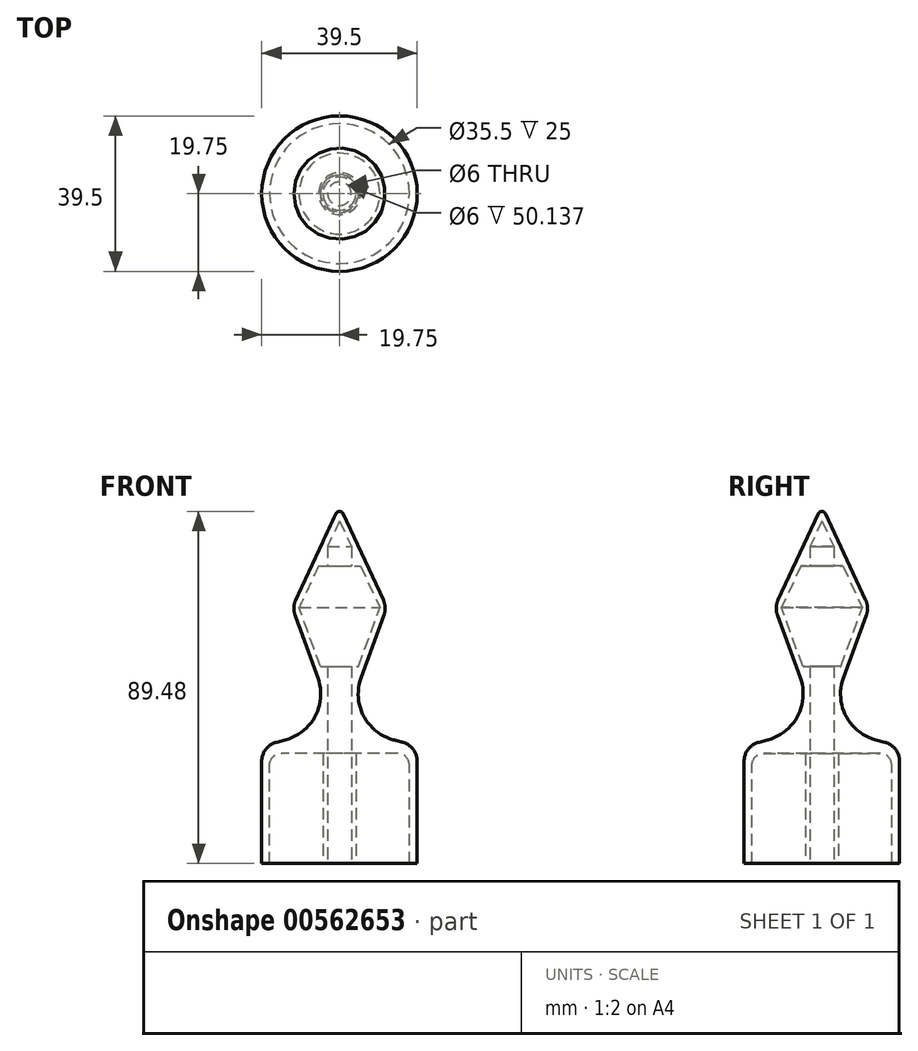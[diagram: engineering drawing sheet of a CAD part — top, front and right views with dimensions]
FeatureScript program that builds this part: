
annotation { "Feature Type Name" : "Feature", "Feature Type Description" : "" }
export const myFeature = defineFeature(function(context is Context, id is Id, definition is map)
    precondition{}
    {
        {
            var Q0;
            Q0=qCreatedBy(makeId("Front.planeOp"),FACE);
            var sketch = newSketch(context, id + "F0", { "sketchPlane" : qUnion([Q0])});
            skLineSegment(sketch, "E0.top", {"start": v(17.75, -35.14) * mm, "end": v(19.75, -35.14) * mm});
            skLineSegment(sketch, "E0.left", {"start": v(0, 0) * mm, "end": v(0, -7.14) * mm});
            skLineSegment(sketch, "E0.right", {"start": v(19.75, -5.3) * mm, "end": v(19.75, -35.14) * mm});
            skLineSegment(sketch, "E1", {"start": v(0, 0) * mm, "end": v(19.75, -5.3) * mm});
            skLineSegment(sketch, "E2.top", {"start": v(0, -7.14) * mm, "end": v(17.75, -7.14) * mm});
            skLineSegment(sketch, "E2.right", {"start": v(17.75, -35.14) * mm, "end": v(17.75, -7.14) * mm});
            skSolve(sketch);
        }
        {
            var Q0;
            Q0=qCreatedBy(makeId("Front.planeOp"),FACE);
            var sketch = newSketch(context, id + "F1", { "sketchPlane" : qUnion([Q0])});
            skLineSegment(sketch, "E3", {"start": v(0, 237.23) * mm, "end": v(0, -268.52) * mm});
            skSolve(sketch);
        }
        {
            var Q0;
            Q0 = qSketchRegion(id + "F0", true);
            var Q1;
            Q1=sQuery(id+"F1.wireOp",EDGE,"E3");
            revolve(context, id + "F2", {"surfaceOperationType" : NewSurfaceOperationType.NEW, "entities" : qUnion([Q0]), "axis" : qUnion([Q1]), "revolveType" : RevolveType.FULL});
        }
        {
            var Q0;
            Q0=qCreatedBy(makeId("Front.planeOp"),FACE);
            var sketch = newSketch(context, id + "F3", { "sketchPlane" : qUnion([Q0])});
            skLineSegment(sketch, "E4", {"start": v(0, -3) * mm, "end": v(0, 54.34) * mm});
            skLineSegment(sketch, "E5", {"start": v(0.9, 53.76) * mm, "end": v(12, 29.97) * mm});
            skLineSegment(sketch, "E6", {"start": v(12, 29.97) * mm, "end": v(0, -3) * mm});
            skArc(sketch, "E7", {"start": v(0.9, 53.76) * mm, "mid": v(0.54, 54.18) * mm, "end": v(0, 54.34) * mm});
            skSolve(sketch);
        }
        {
            var Q0;
            Q0 = qSketchRegion(id + "F3", true);
            var Q1;
            Q1=sQuery(id+"F3.wireOp",EDGE,"E4");
            revolve(context, id + "F4", {"operationType" : NewBodyOperationType.ADD, "surfaceOperationType" : NewSurfaceOperationType.NEW, "entities" : qUnion([Q0]), "axis" : qUnion([Q1]), "revolveType" : RevolveType.FULL});
        }
        {
            var Q0;
            Q0=makeQuery(id+"F4.boolean.opBoolean","INTERSECT",EDGE,{"derivedFrom":[makeQuery(id+"F2.opRevolve","SWEPT_FACE",FACE,{"disambiguationData":[OSD([sQuery(id+"F0.wireOp",EDGE,"E1")])]}),makeQuery(id+"F4.opRevolve","SWEPT_FACE",FACE,{"disambiguationData":[OSD([sQuery(id+"F3.wireOp",EDGE,"E6")])]})]});
            fillet(context, id + "F5", {"entities" : qUnion([Q0]), "tangentPropagation" : true, "radius" : 12 * mm, "defaultsChanged" : true, "vertexSettings" : [], "allowEdgeOverflow" : false});
        }
        {
            var Q0;
            Q0=makeQuery(id+"F4.opRevolve","SWEPT_EDGE",EDGE,{"disambiguationData":[OSD([sQuery(id+"F3.wireOp",EDGE,"E5"),sQuery(id+"F3.wireOp",EDGE,"E6")])]});
            var Q1;
            Q1=makeQuery(id+"F2.opRevolve","SWEPT_EDGE",EDGE,{"disambiguationData":[OSD([sQuery(id+"F0.wireOp",EDGE,"E0.right"),sQuery(id+"F0.wireOp",EDGE,"E1")])]});
            fillet(context, id + "F6", {"entities" : qUnion([Q0, Q1]), "tangentPropagation" : true, "radius" : 5 * mm, "defaultsChanged" : true, "vertexSettings" : [], "allowEdgeOverflow" : false});
        }
        {
            var Q0;
            Q0=qCreatedBy(makeId("Front.planeOp"),FACE);
            var sketch = newSketch(context, id + "F7", { "sketchPlane" : qUnion([Q0])});
            skLineSegment(sketch, "E8", {"start": v(0, 51.92) * mm, "end": v(3, 45.48) * mm});
            skLineSegment(sketch, "E9", {"start": v(10.27, 29.9) * mm, "end": v(4.85, 15) * mm});
            skLineSegment(sketch, "E10", {"start": v(3, 15) * mm, "end": v(3, -35.14) * mm});
            skLineSegment(sketch, "E11", {"start": v(3, -35.14) * mm, "end": v(0, -35.14) * mm});
            skLineSegment(sketch, "E12", {"start": v(0, 51.92) * mm, "end": v(0, -35.14) * mm});
            skLineSegment(sketch, "E13", {"start": v(3, 15) * mm, "end": v(4.85, 15) * mm});
            skLineSegment(sketch, "E14", {"start": v(3, 45.48) * mm, "end": v(3, 40.48) * mm});
            skLineSegment(sketch, "E15", {"start": v(3, 40.48) * mm, "end": v(5.33, 40.48) * mm});
            skLineSegment(sketch, "E16.trimOffspring", {"start": v(5.33, 40.48) * mm, "end": v(10.27, 29.9) * mm});
            skSolve(sketch);
        }
        {
            var Q0;
            Q0 = qSketchRegion(id + "F7", true);
            var Q1;
            Q1=sQuery(id+"F1.wireOp",EDGE,"E3");
            revolve(context, id + "F8", {"operationType" : NewBodyOperationType.REMOVE, "surfaceOperationType" : NewSurfaceOperationType.NEW, "entities" : qUnion([Q0]), "axis" : qUnion([Q1]), "revolveType" : RevolveType.FULL, "oppositeDirection" : true});
        }
        {
            var Q0;
            Q0=makeQuery(id+"F2.opRevolve","SWEPT_FACE",FACE,{"disambiguationData":[OSD([sQuery(id+"F0.wireOp",EDGE,"E0.top")])]});
            var sketch = newSketch(context, id + "F9", { "sketchPlane" : qUnion([Q0])});
            skCircle(sketch, "E17", {"center": v(0, 0) * mm, "radius": 4.2 * mm});
            skCircle(sketch, "E18", {"center": v(0, 0) * mm, "radius": 3 * mm});
            skSolve(sketch);
        }
        {
            var Q0;
            Q0 = qSketchRegion(id + "F9", true);
            extrude(context, id + "F10", {"entities" : qUnion([Q0]), "operationType" : NewBodyOperationType.ADD, "endBound" : BoundingType.UP_TO_NEXT, "oppositeDirection" : true, "depth" : 25 * mm, "offsetDistance" : 25 * mm});
        }
        {
            var Q0;
            Q0=makeQuery(id+"F2.opRevolve","SWEPT_EDGE",EDGE,{"disambiguationData":[OSD([sQuery(id+"F0.wireOp",EDGE,"E2.top"),sQuery(id+"F0.wireOp",EDGE,"E2.right")])]});
            var Q1;
            Q1=makeQuery(id+"F10.opExtrude","CAP_EDGE",EDGE,{"disambiguationData":[OSD([sQuery(id+"F9.wireOp",EDGE,"E17")])],"isStart":false});
            fillet(context, id + "F11", {"entities" : qUnion([Q0, Q1]), "tangentPropagation" : true, "radius" : 3 * mm, "defaultsChanged" : true, "vertexSettings" : [], "allowEdgeOverflow" : false});
        }
    });
